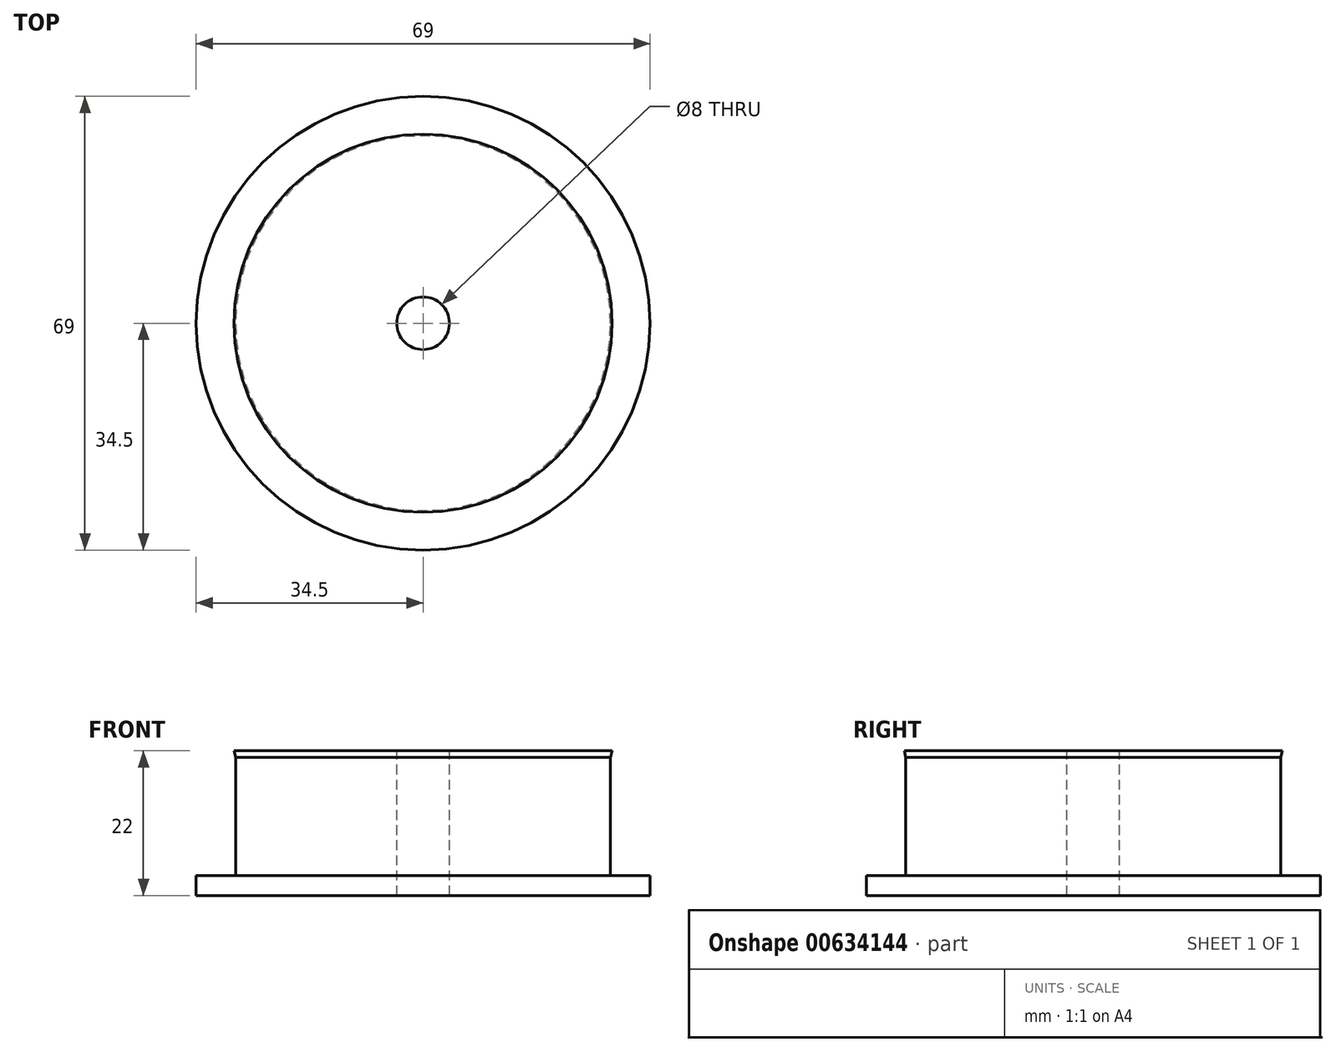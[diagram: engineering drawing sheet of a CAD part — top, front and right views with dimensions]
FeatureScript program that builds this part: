
annotation { "Feature Type Name" : "Feature", "Feature Type Description" : "" }
export const myFeature = defineFeature(function(context is Context, id is Id, definition is map)
    precondition{}
    {
        {
            var Q0;
            Q0=qCreatedBy(makeId("Front.planeOp"),FACE);
            var sketch = newSketch(context, id + "F0", { "sketchPlane" : qUnion([Q0])});
            skLineSegment(sketch, "E0", {"start": v(4, 29.66) * mm, "end": v(4, -27.95) * mm, "construction": true});
            skLineSegment(sketch, "E1", {"start": v(4, 0.86) * mm, "end": v(34.5, 0.86) * mm});
            skLineSegment(sketch, "E2", {"start": v(34.5, 0.86) * mm, "end": v(34.5, 3.86) * mm});
            skLineSegment(sketch, "E3", {"start": v(34.5, 3.86) * mm, "end": v(28.5, 3.86) * mm});
            skLineSegment(sketch, "E4", {"start": v(28.5, 3.86) * mm, "end": v(28.5, 21.86) * mm});
            skLineSegment(sketch, "E5", {"start": v(28.75, 22.86) * mm, "end": v(28.5, 22.86) * mm});
            skLineSegment(sketch, "E6", {"start": v(28.5, 22.86) * mm, "end": v(4, 22.86) * mm});
            skLineSegment(sketch, "E7", {"start": v(4, 22.86) * mm, "end": v(4, 0.86) * mm});
            skLineSegment(sketch, "E8", {"start": v(0, 29.66) * mm, "end": v(0, -27.95) * mm, "construction": true});
            skLineSegment(sketch, "E9", {"start": v(28.75, 22.86) * mm, "end": v(28.5, 21.86) * mm});
            skLineSegment(sketch, "E10", {"start": v(29.63, 49.9) * mm, "end": v(30.21, 49.75) * mm});
            skSolve(sketch);
        }
        {
            var Q0;
            Q0 = qSketchRegion(id + "F0", true);
            var Q1;
            Q1=sQuery(id+"F0.wireOp",EDGE,"E8");
            revolve(context, id + "F1", {"entities" : qUnion([Q0]), "axis" : qUnion([Q1]), "revolveType" : RevolveType.FULL});
        }
    });
